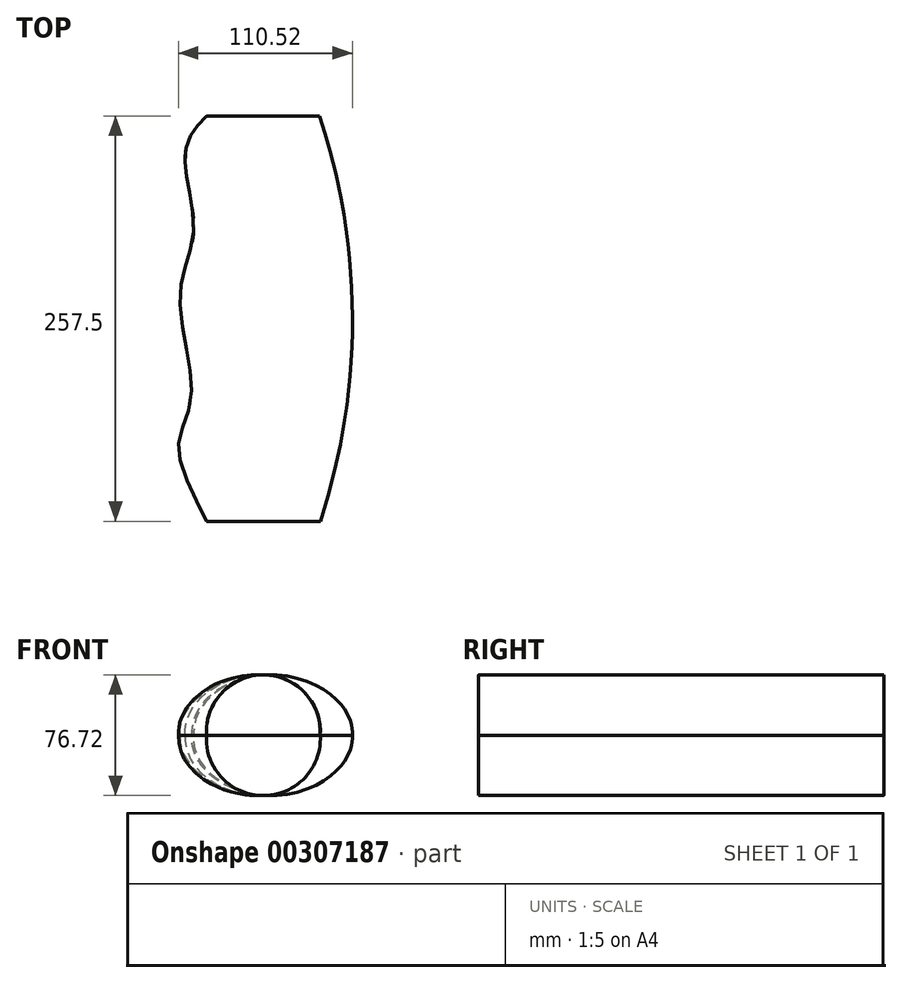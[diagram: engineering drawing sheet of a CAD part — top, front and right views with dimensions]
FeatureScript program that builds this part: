
annotation { "Feature Type Name" : "Feature", "Feature Type Description" : "" }
export const myFeature = defineFeature(function(context is Context, id is Id, definition is map)
    precondition{}
    {
        {
            var Q0;
            Q0=qCreatedBy(makeId("Front.planeOp"),FACE);
            var sketch = newSketch(context, id + "F0", { "sketchPlane" : qUnion([Q0])});
            skArc(sketch, "E0", {"start": v(71.77, 0) * mm, "mid": v(35.88, 38.35) * mm, "end": v(0, 0) * mm});
            skSolve(sketch);
        }
        {
            var Q0;
            Q0=qCreatedBy(makeId("Front.planeOp"),FACE);
            cPlane(context, id + "F1", {"entities" : qUnion([Q0]), "cplaneType" : CPlaneType.OFFSET, "offset" : 257.5 * mm, "width" : 150 * mm, "height" : 150 * mm});
        }
        {
            var Q0;
            Q0=qCreatedBy(id+"F1.planeOp",FACE);
            var sketch = newSketch(context, id + "F2", { "sketchPlane" : qUnion([Q0])});
            skArc(sketch, "E1", {"start": v(72.3, 0) * mm, "mid": v(36.15, 38.36) * mm, "end": v(0, 0) * mm});
            skSolve(sketch);
        }
        {
            var Q0;
            Q0=qCreatedBy(makeId("Top.planeOp"),FACE);
            var sketch = newSketch(context, id + "F3", { "sketchPlane" : qUnion([Q0])});
            skFitSpline(sketch, "E2", {"points": [v(0, 0) * mm, v(-13.26, -22.5) * mm, v(-8.04, -72.38) * mm, v(-16.73, -113.17) * mm, v(-9.63, -178.97) * mm, v(-17.75, -210.28) * mm, v(0, -257.5) * mm], "startDerivative": vector(-137.47, -144.55) * mm, "endDerivative": vector(119.7, -253.28) * mm});
            skArc(sketch, "E3", {"start": v(72.3, -257.5) * mm, "mid": v(92.68, -128.7) * mm, "end": v(71.77, 0) * mm});
            skSolve(sketch);
        }
        {
            var Q0;
            Q0=sQuery(id+"F0.wireOp",EDGE,"E0");
            var Q1;
            Q1=sQuery(id+"F2.wireOp",EDGE,"E1");
            var Q2;
            Q2=sQuery(id+"F3.wireOp",EDGE,"E3");
            var Q3;
            Q3=sQuery(id+"F3.wireOp",EDGE,"E2");
            loft(context, id + "F4", {"bodyType" : ToolBodyType.SURFACE, "addGuides" : true, "wireProfilesArray" : [{ "wireProfileEntities" : qUnion([Q0]) }, { "wireProfileEntities" : qUnion([Q1]) }], "guidesArray" : [{ "guideEntities" : qUnion([Q2]), "guideDerivativeType" : LoftGuideDerivativeType.DEFAULT, "guideDerivativeMagnitude" : 1 }, { "guideEntities" : qUnion([Q3]), "guideDerivativeType" : LoftGuideDerivativeType.DEFAULT, "guideDerivativeMagnitude" : 1 }]});
        }
        {
            var Q0;
            Q0=qCreatedBy(makeId("Top.planeOp"),FACE);
            var sketch = newSketch(context, id + "F5", { "sketchPlane" : qUnion([Q0])});
            skLineSegment(sketch, "E4", {"start": v(0, -257.5) * mm, "end": v(72.3, -257.5) * mm});
            skLineSegment(sketch, "E5", {"start": v(0, 0) * mm, "end": v(71.77, 0) * mm});
            skSolve(sketch);
        }
        {
            var Q0;
            Q0=makeQuery(id+"F4.opLoft","MID_CAP_EDGE",EDGE,{"disambiguationData":[OSD([sQuery(id+"F0.wireOp",VERTEX,"E0.start"),sQuery(id+"F0.wireOp",VERTEX,"E0.end"),sQuery(id+"F0.wireOp",EDGE,"E0")])],"capPos":0.0});
            var Q1;
            Q1=sQuery(id+"F5.wireOp",EDGE,"E5");
            loft(context, id + "F6", {"bodyType" : ToolBodyType.SURFACE, "wireProfilesArray" : [{ "wireProfileEntities" : qUnion([Q0]) }, { "wireProfileEntities" : qUnion([Q1]) }]});
        }
        {
            var Q0;
            Q0=qCreatedBy(id+"F1.planeOp",FACE);
            var sketch = newSketch(context, id + "F7", { "sketchPlane" : qUnion([Q0])});
            skLineSegment(sketch, "E6", {"start": v(72.3, 0) * mm, "end": v(0, 0) * mm});
            skSolve(sketch);
        }
        {
            var Q0;
            Q0=makeQuery(id+"F4.opLoft","MID_CAP_EDGE",EDGE,{"disambiguationData":[OSD([sQuery(id+"F2.wireOp",VERTEX,"E1.start"),sQuery(id+"F2.wireOp",VERTEX,"E1.end"),sQuery(id+"F2.wireOp",EDGE,"E1")])],"capPos":1.0});
            var Q1;
            Q1=sQuery(id+"F7.wireOp",EDGE,"E6");
            loft(context, id + "F8", {"bodyType" : ToolBodyType.SURFACE, "wireProfilesArray" : [{ "wireProfileEntities" : qUnion([Q0]) }, { "wireProfileEntities" : qUnion([Q1]) }]});
        }
        {
            var Q0;
            Q0=makeQuery(id+"F4.opLoft","SWEPT_BODY",BODY,{"disambiguationData":[OSD([sQuery(id+"F0.wireOp",EDGE,"E0"),sQuery(id+"F2.wireOp",EDGE,"E1"),sQuery(id+"F3.wireOp",EDGE,"E2"),sQuery(id+"F3.wireOp",EDGE,"E3")])]});
            var Q1;
            Q1=makeQuery(id+"F6.opLoft","SWEPT_BODY",BODY,{"disambiguationData":[OSD([sQuery(id+"F0.wireOp",EDGE,"E0"),sQuery(id+"F3.wireOp",EDGE,"E2"),sQuery(id+"F3.wireOp",EDGE,"E3"),sQuery(id+"F5.wireOp",EDGE,"E5")])]});
            var Q2;
            Q2=makeQuery(id+"F8.opLoft","SWEPT_BODY",BODY,{"disambiguationData":[OSD([sQuery(id+"F2.wireOp",EDGE,"E1"),sQuery(id+"F3.wireOp",EDGE,"E2"),sQuery(id+"F3.wireOp",EDGE,"E3"),sQuery(id+"F7.wireOp",EDGE,"E6")])]});
            var Q3;
            Q3=qCreatedBy(makeId("Top.planeOp"),FACE);
            mirror(context, id + "F9", {"entities" : qUnion([Q0, Q1, Q2]), "mirrorPlane" : qUnion([Q3])});
        }
    });
